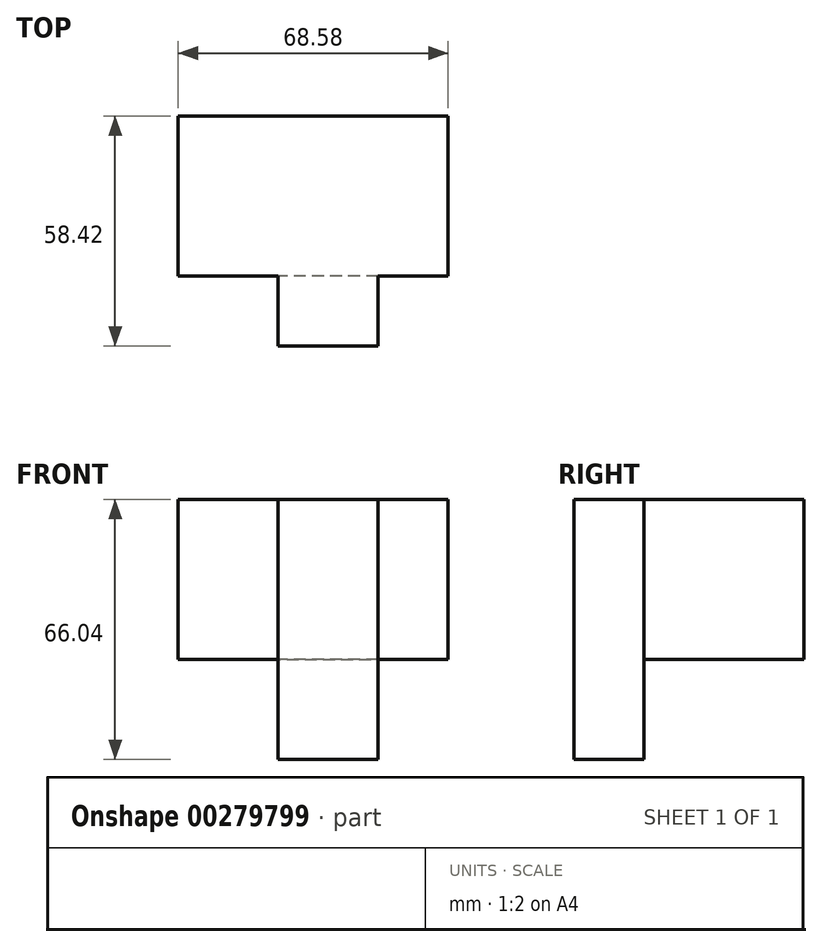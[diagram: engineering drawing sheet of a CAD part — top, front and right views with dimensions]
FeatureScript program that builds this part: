
annotation { "Feature Type Name" : "Feature", "Feature Type Description" : "" }
export const myFeature = defineFeature(function(context is Context, id is Id, definition is map)
    precondition{}
    {
        {
            var Q0;
            Q0=qCreatedBy(makeId("Right.planeOp"),FACE);
            var sketch = newSketch(context, id + "F0", { "sketchPlane" : qUnion([Q0])});
            skLineSegment(sketch, "E0.bottom", {"start": v(-58.52, 40.88) * mm, "end": v(-17.88, 40.88) * mm});
            skLineSegment(sketch, "E0.top", {"start": v(-58.52, 0.24) * mm, "end": v(-17.88, 0.24) * mm});
            skLineSegment(sketch, "E0.left", {"start": v(-58.52, 40.88) * mm, "end": v(-58.52, 0.24) * mm});
            skLineSegment(sketch, "E0.right", {"start": v(-17.88, 40.88) * mm, "end": v(-17.88, 0.24) * mm});
            skSolve(sketch);
        }
        {
            var Q0;
            Q0=makeQuery(id+"F0.imprint","IMPRINT",FACE,{"disambiguationData":[TD([[makeQuery(id+"F0.imprint","IMPRINT",EDGE,{"derivedFrom":sQuery(id+"F0.wireOp",EDGE,"E0.bottom")}),-1.0]])]});
            extrude(context, id + "F1", {"entities" : qUnion([Q0]), "oppositeDirection" : true, "depth" : 68.58 * mm});
        }
        {
            var Q0;
            Q0=makeQuery(id+"F1.opExtrude","SWEPT_FACE",FACE,{"disambiguationData":[OSD([sQuery(id+"F0.wireOp",EDGE,"E0.left")])]});
            var sketch = newSketch(context, id + "F2", { "sketchPlane" : qUnion([Q0])});
            skLineSegment(sketch, "E1", {"start": v(-17.78, 40.88) * mm, "end": v(-17.78, 0) * mm});
            skLineSegment(sketch, "E2", {"start": v(-43.18, 40.88) * mm, "end": v(-43.18, 0.24) * mm});
            skSolve(sketch);
        }
        {
            var Q0;
            {var subQ6=sQuery(id+"F2.wireOp",EDGE,"E2");Q0=makeQuery(id+"F2.imprint","IMPRINT",FACE,{"disambiguationData":[TD([[makeQuery(id+"F2.imprint","IMPRINT",EDGE,{"derivedFrom":subQ6}),1.0]])]});}
            extrude(context, id + "F3", {"entities" : qUnion([Q0]), "operationType" : NewBodyOperationType.ADD, "depth" : 17.78 * mm});
        }
        {
            var Q0;
            {var subQ0=sQuery(id+"F0.wireOp",EDGE,"E0.top");Q0=makeQuery(id+"F3.boolean.opBoolean","MERGE",FACE,{"derivedFrom":[makeQuery(id+"F1.opExtrude","SWEPT_FACE",FACE,{"disambiguationData":[OSD([subQ0])]}),makeQuery(id+"F3.opExtrude","SWEPT_FACE",FACE,{"disambiguationData":[OSD([subQ0,sQuery(id+"F0.wireOp",EDGE,"E0.left")])]})]});}
            var sketch = newSketch(context, id + "F4", { "sketchPlane" : qUnion([Q0])});
            skLineSegment(sketch, "E3", {"start": v(-17.78, 58.52) * mm, "end": v(-43.18, 58.52) * mm});
            skSolve(sketch);
        }
        {
            var Q0;
            Q0=makeQuery(id+"F4.imprint","IMPRINT",FACE,{"disambiguationData":[TD([[makeQuery(id+"F4.imprint","IMPRINT",EDGE,{"derivedFrom":sQuery(id+"F4.wireOp",EDGE,"E3")}),-1.0]])]});
            extrude(context, id + "F5", {"entities" : qUnion([Q0]), "operationType" : NewBodyOperationType.ADD, "depth" : 25.4 * mm});
        }
    });
